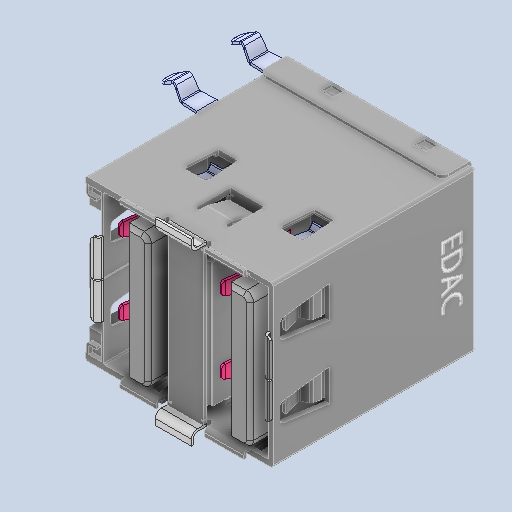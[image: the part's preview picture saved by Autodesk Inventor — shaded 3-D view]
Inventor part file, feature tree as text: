
AUTODESK INVENTOR PART (.ipt)
format: ipt  version: 2024.3 (Build 283343000, 343)  size: 1,649,664 bytes
history: native  units: in
note: dims shown in document units (in); Inventor stores cm internally (conversion verified against a paired STEP export)
features: other x19, mirror x7, fillet x4, chamfer x2
ambient origin geometry x8: Origin, YZ Plane, XZ Plane, XY Plane, X Axis, Y Axis, Z Axis, Center Point
bodies: Solid1 (feature_tree), Solid2 (feature_tree), Solid3 (feature_tree), Solid4 (feature_tree), Solid5 (feature_tree), Solid6 (feature_tree), Solid7 (feature_tree), Solid8 (feature_tree), Solid9 (feature_tree), Solid10 (feature_tree), Solid11 (feature_tree), Solid12 (feature_tree), Solid13 (feature_tree), Solid14 (feature_tree), Solid15 (feature_tree), Solid16 (feature_tree), Solid17 (feature_tree), Solid18 (feature_tree), Solid19 (feature_tree), Solid20 (feature_tree), Solid21 (feature_tree), Solid22 (feature_tree), Solid23 (feature_tree), Solid24 (feature_tree), Solid25 (feature_tree), Solid26 (feature_tree), Solid27 (feature_tree), Solid28 (feature_tree), Solid29 (feature_tree), Solid30 (feature_tree), Solid31 (feature_tree), Solid32 (feature_tree), Solid33 (feature_tree)
feature tree (32):
  other  "Cut-Extrude5[1]"
  other  "Cut-Extrude5[2]"
  other  "Cut-Extrude5[3]"
  other  "Cut-Extrude5[4]"
  other  "Cut-Extrude7[1]"
  other  "Cut-Extrude7[2]"
  other  "Cut-Extrude11[3]"
  other  "Cut-Extrude11[4]"
  mirror  "Mirror7[1]"
  mirror  "Mirror7[2]"
  other  "Cut-Extrude13[1]"
  other  "Cut-Extrude13[2]"
  mirror  "Mirror8[1]"
  mirror  "Mirror8[2]"
  chamfer  "Chamfer5"  [1 undecoded]
  chamfer  "Chamfer4"  [1 undecoded]
  other  "Boss-Extrude14"
  other  "LPattern1"
  mirror  "Mirror9[1]"
  mirror  "Mirror9[2]"
  other  "LPattern2[1]"
  other  "LPattern2[2]"
  other  "LPattern2[3]"
  other  "LPattern2[4]"
  other  "LPattern3[1]"
  other  "LPattern3[2]"
  other  "Cut-Extrude15"
  mirror  "Mirror10"
  fillet  "Fillet6"  [1 undecoded]
  fillet  "Fillet7"  [1 undecoded]
  fillet  "Fillet5"  [1 undecoded]
  fillet  "Fillet4"  [1 undecoded]
note: 6 required parameter values undecoded (feature->parameter linkage not recoverable at this tier; creation-order binding heuristic only, values carry confidence <= 0.55)
